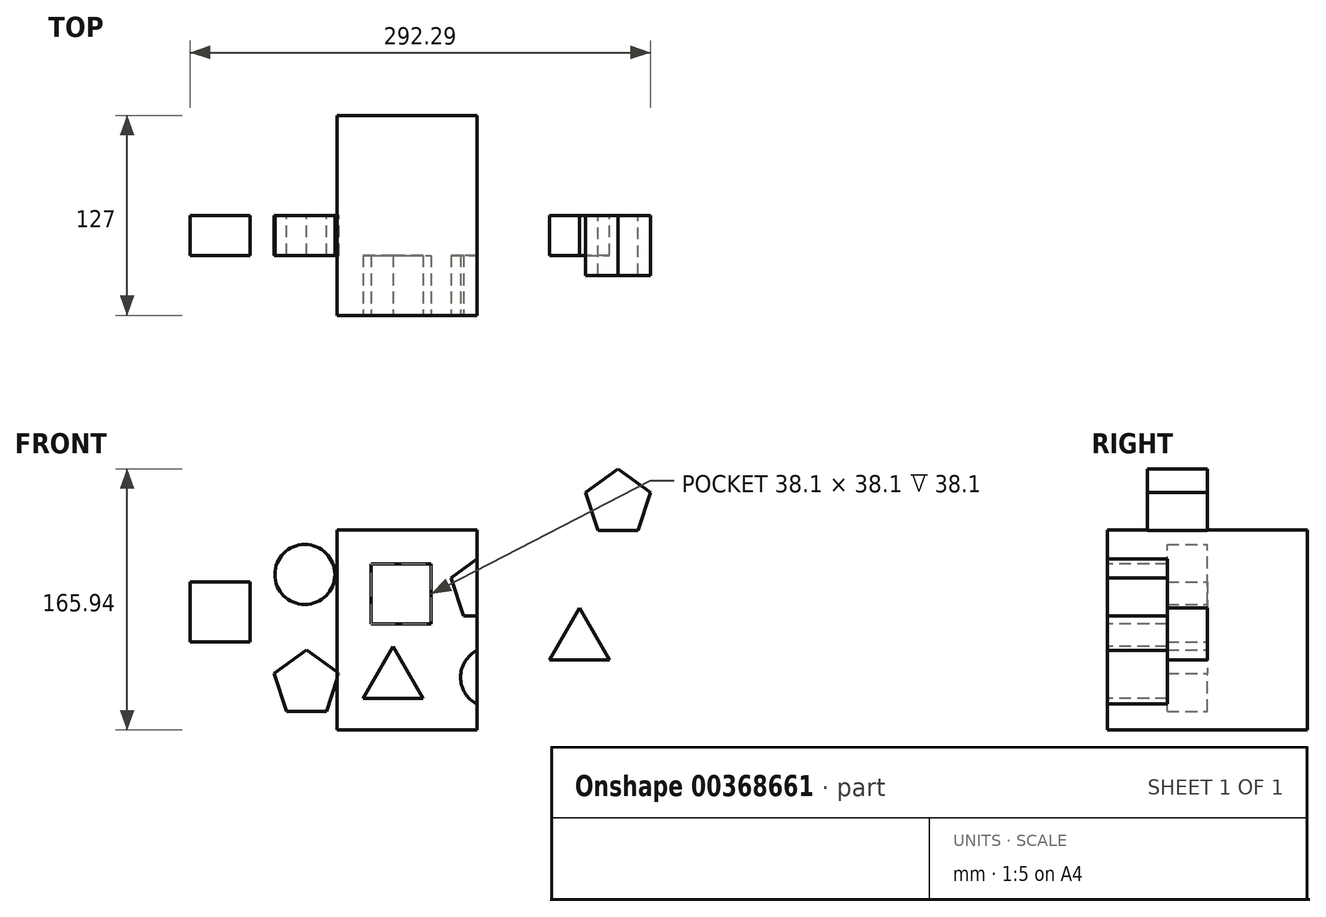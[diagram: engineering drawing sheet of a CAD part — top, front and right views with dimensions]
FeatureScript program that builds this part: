
annotation { "Feature Type Name" : "Feature", "Feature Type Description" : "" }
export const myFeature = defineFeature(function(context is Context, id is Id, definition is map)
    precondition{}
    {
        {
            var Q0;
            Q0=qCreatedBy(makeId("Front.planeOp"),FACE);
            var sketch = newSketch(context, id + "F0", { "sketchPlane" : qUnion([Q0])});
            skLineSegment(sketch, "E0.bottom", {"start": v(-62.46, 62.67) * mm, "end": v(64.54, 62.67) * mm});
            skLineSegment(sketch, "E0.top", {"start": v(-62.46, -64.33) * mm, "end": v(64.54, -64.33) * mm});
            skLineSegment(sketch, "E0.left", {"start": v(-62.46, 62.67) * mm, "end": v(-62.46, -64.33) * mm});
            skLineSegment(sketch, "E0.right", {"start": v(64.54, 62.67) * mm, "end": v(64.54, -64.33) * mm});
            skSolve(sketch);
        }
        {
            var Q0;
            Q0 = qSketchRegion(id + "F0", true);
            extrude(context, id + "F1", {"entities" : qUnion([Q0]), "endBound" : BoundingType.SYMMETRIC, "depth" : 127 * mm});
        }
        {
            var Q0;
            Q0=makeQuery(id+"F1.opExtrude","CAP_FACE",FACE,{"disambiguationData":[OSD([sQuery(id+"F0.wireOp",EDGE,"E0.bottom"),sQuery(id+"F0.wireOp",EDGE,"E0.top"),sQuery(id+"F0.wireOp",EDGE,"E0.left"),sQuery(id+"F0.wireOp",EDGE,"E0.right")])],"isStart":false});
            var sketch = newSketch(context, id + "F2", { "sketchPlane" : qUnion([Q0])});
            skLineSegment(sketch, "E1.bottom", {"start": v(-40.71, 41.18) * mm, "end": v(-2.61, 41.18) * mm});
            skLineSegment(sketch, "E1.top", {"start": v(-40.71, 3.08) * mm, "end": v(-2.61, 3.08) * mm});
            skLineSegment(sketch, "E1.left", {"start": v(-40.71, 41.18) * mm, "end": v(-40.71, 3.08) * mm});
            skLineSegment(sketch, "E1.right", {"start": v(-2.61, 41.18) * mm, "end": v(-2.61, 3.08) * mm});
            skSolve(sketch);
        }
        {
            var Q0;
            Q0 = qSketchRegion(id + "F2", true);
            var Q1;
            Q1 = qSketchRegion(id + "FlVycBwDndMsINd_1", true);
            extrude(context, id + "F3", {"entities" : qUnion([Q0, Q1]), "operationType" : NewBodyOperationType.REMOVE, "oppositeDirection" : true, "depth" : 38.1 * mm});
        }
        {
            var Q0;
            Q0=makeQuery(id+"F1.opExtrude","CAP_FACE",FACE,{"disambiguationData":[OSD([sQuery(id+"F0.wireOp",EDGE,"E0.bottom"),sQuery(id+"F0.wireOp",EDGE,"E0.top"),sQuery(id+"F0.wireOp",EDGE,"E0.left"),sQuery(id+"F0.wireOp",EDGE,"E0.right")])],"isStart":false});
            var sketch = newSketch(context, id + "F4", { "sketchPlane" : qUnion([Q0])});
            skCircle(sketch, "E2.cCircle", {"center": v(30.55, 25.74) * mm, "radius": 17.48 * mm, "construction": true});
            skLineSegment(sketch, "E2.0", {"start": v(51.1, 32.42) * mm, "end": v(43.25, 8.26) * mm});
            skLineSegment(sketch, "E2.1", {"start": v(43.25, 8.26) * mm, "end": v(17.85, 8.26) * mm});
            skLineSegment(sketch, "E2.2", {"start": v(17.85, 8.26) * mm, "end": v(10, 32.42) * mm});
            skLineSegment(sketch, "E2.3", {"start": v(10, 32.42) * mm, "end": v(30.55, 47.35) * mm});
            skLineSegment(sketch, "E2.4", {"start": v(30.55, 47.35) * mm, "end": v(51.1, 32.42) * mm});
            skPoint(sketch, "E2.0.midPoint", {"position": v(47.18, 20.34) * mm});
            skSolve(sketch);
        }
        {
            var Q0;
            Q0 = qSketchRegion(id + "F4", true);
            extrude(context, id + "F5", {"entities" : qUnion([Q0]), "operationType" : NewBodyOperationType.REMOVE, "oppositeDirection" : true, "depth" : 38.1 * mm});
        }
        {
            var Q0;
            Q0=makeQuery(id+"F1.opExtrude","CAP_FACE",FACE,{"disambiguationData":[OSD([sQuery(id+"F0.wireOp",EDGE,"E0.bottom"),sQuery(id+"F0.wireOp",EDGE,"E0.top"),sQuery(id+"F0.wireOp",EDGE,"E0.left"),sQuery(id+"F0.wireOp",EDGE,"E0.right")])],"isStart":false});
            var sketch = newSketch(context, id + "F6", { "sketchPlane" : qUnion([Q0])});
            skCircle(sketch, "E3", {"center": v(35.03, -30.79) * mm, "radius": 19.05 * mm});
            skLineSegment(sketch, "E4", {"start": v(-45.98, -44.07) * mm, "end": v(-7.88, -44.07) * mm});
            skLineSegment(sketch, "E5", {"start": v(-7.88, -44.07) * mm, "end": v(-26.93, -11.08) * mm});
            skLineSegment(sketch, "E6", {"start": v(-26.93, -11.08) * mm, "end": v(-45.98, -44.07) * mm});
            skSolve(sketch);
        }
        {
            var Q0;
            Q0=makeQuery(id+"F6.imprint","IMPRINT",FACE,{"disambiguationData":[TD([[makeQuery(id+"F6.imprint","IMPRINT",EDGE,{"derivedFrom":makeQuery(id+"F5.boolean.opBoolean","COPY",EDGE,{"derivedFrom":makeQuery(id+"F5.opExtrude","CAP_EDGE",EDGE,{"disambiguationData":[OSD([sQuery(id+"F4.wireOp",EDGE,"E2.0")])],"isStart":true})})}),-1.0]])]});
            var Q1;
            Q1=makeQuery(id+"F6.imprint","IMPRINT",FACE,{"disambiguationData":[TD([[makeQuery(id+"F6.imprint","IMPRINT",EDGE,{"derivedFrom":makeQuery(id+"F3.boolean.opBoolean","COPY",EDGE,{"derivedFrom":makeQuery(id+"F3.opExtrude","CAP_EDGE",EDGE,{"disambiguationData":[OSD([sQuery(id+"F2.wireOp",EDGE,"E1.bottom")])],"isStart":true})})}),-1.0]])]});
            var Q2;
            Q2=makeQuery(id+"F1.opExtrude","SWEPT_FACE",FACE,{"disambiguationData":[OSD([sQuery(id+"F0.wireOp",EDGE,"E0.right")])]});
            var Q3;
            Q3=makeQuery(id+"F6.imprint","IMPRINT",FACE,{"disambiguationData":[TD([[makeQuery(id+"F6.imprint","IMPRINT",EDGE,{"derivedFrom":sQuery(id+"F6.wireOp",EDGE,"D8XwbJ4F-R5Sw-1uv0-skdv-VhJgHIrJsN8F")}),1.0]])]});
            extrude(context, id + "F7", {"entities" : qUnion([Q0, Q1, Q2, Q3]), "operationType" : NewBodyOperationType.REMOVE, "oppositeDirection" : true, "depth" : 38.1 * mm});
        }
        {
            var Q0;
            Q0 = qSketchRegion(id + "F6", true);
            extrude(context, id + "F8", {"entities" : qUnion([Q0]), "operationType" : NewBodyOperationType.REMOVE, "oppositeDirection" : true, "depth" : 38.1 * mm});
        }
        {
            var Q0;
            Q0 = qSketchRegion(id + "F6", true);
            extrude(context, id + "F9", {"entities" : qUnion([Q0]), "operationType" : NewBodyOperationType.REMOVE, "oppositeDirection" : true, "depth" : 38.1 * mm});
        }
        {
            var Q0;
            Q0=qCreatedBy(makeId("Front.planeOp"),FACE);
            var sketch = newSketch(context, id + "F10", { "sketchPlane" : qUnion([Q0])});
            skLineSegment(sketch, "E7.bottom", {"start": v(-155.72, 29.9) * mm, "end": v(-117.62, 29.9) * mm});
            skLineSegment(sketch, "E7.top", {"start": v(-155.72, -8.2) * mm, "end": v(-117.62, -8.2) * mm});
            skLineSegment(sketch, "E7.left", {"start": v(-155.72, 29.9) * mm, "end": v(-155.72, -8.2) * mm});
            skLineSegment(sketch, "E7.right", {"start": v(-117.62, 29.9) * mm, "end": v(-117.62, -8.2) * mm});
            skSolve(sketch);
        }
        {
            var Q0;
            Q0 = qSketchRegion(id + "F10", true);
            extrude(context, id + "F11", {"entities" : qUnion([Q0]), "depth" : 25.4 * mm});
        }
        {
            var Q0;
            Q0=qCreatedBy(makeId("Front.planeOp"),FACE);
            var sketch = newSketch(context, id + "F12", { "sketchPlane" : qUnion([Q0])});
            skCircle(sketch, "E8.cCircle", {"center": v(-81.84, -34.97) * mm, "radius": 17.48 * mm, "construction": true});
            skLineSegment(sketch, "E8.0", {"start": v(-94.54, -52.45) * mm, "end": v(-102.39, -28.3) * mm});
            skLineSegment(sketch, "E8.1", {"start": v(-102.39, -28.3) * mm, "end": v(-81.84, -13.36) * mm});
            skLineSegment(sketch, "E8.2", {"start": v(-81.84, -13.36) * mm, "end": v(-61.29, -28.3) * mm});
            skLineSegment(sketch, "E8.3", {"start": v(-61.29, -28.3) * mm, "end": v(-69.14, -52.45) * mm});
            skLineSegment(sketch, "E8.4", {"start": v(-69.14, -52.45) * mm, "end": v(-94.54, -52.45) * mm});
            skPoint(sketch, "E8.0.midPoint", {"position": v(-98.46, -40.37) * mm});
            skCircle(sketch, "E9", {"center": v(-82.9, 34.47) * mm, "radius": 19.05 * mm});
            skLineSegment(sketch, "E10", {"start": v(72.46, -19.69) * mm, "end": v(110.56, -19.69) * mm});
            skLineSegment(sketch, "E11", {"start": v(110.56, -19.69) * mm, "end": v(91.5, 13.31) * mm});
            skLineSegment(sketch, "E12", {"start": v(91.5, 13.31) * mm, "end": v(72.46, -19.69) * mm});
            skSolve(sketch);
        }
        {
            var Q0;
            Q0 = qSketchRegion(id + "F12", true);
            extrude(context, id + "F13", {"entities" : qUnion([Q0]), "depth" : 25.4 * mm});
        }
        {
            var Q0;
            Q0 = qSketchRegion(id + "F12", true);
            extrude(context, id + "F14", {"entities" : qUnion([Q0]), "depth" : 25.4 * mm});
        }
        {
            var Q0;
            Q0=qCreatedBy(makeId("Front.planeOp"),FACE);
            var sketch = newSketch(context, id + "F15", { "sketchPlane" : qUnion([Q0])});
            skLineSegment(sketch, "E13.0", {"start": v(136.57, 86.68) * mm, "end": v(128.72, 62.52) * mm});
            skLineSegment(sketch, "E13.1", {"start": v(128.72, 62.52) * mm, "end": v(103.32, 62.52) * mm});
            skLineSegment(sketch, "E13.2", {"start": v(103.32, 62.52) * mm, "end": v(95.47, 86.68) * mm});
            skLineSegment(sketch, "E13.3", {"start": v(95.47, 86.68) * mm, "end": v(116.02, 101.6) * mm});
            skLineSegment(sketch, "E13.4", {"start": v(116.02, 101.6) * mm, "end": v(136.57, 86.68) * mm});
            skSolve(sketch);
        }
        {
            var Q0;
            Q0 = qSketchRegion(id + "F15", true);
            extrude(context, id + "F16", {"entities" : qUnion([Q0]), "depth" : 38.1 * mm});
        }
    });
